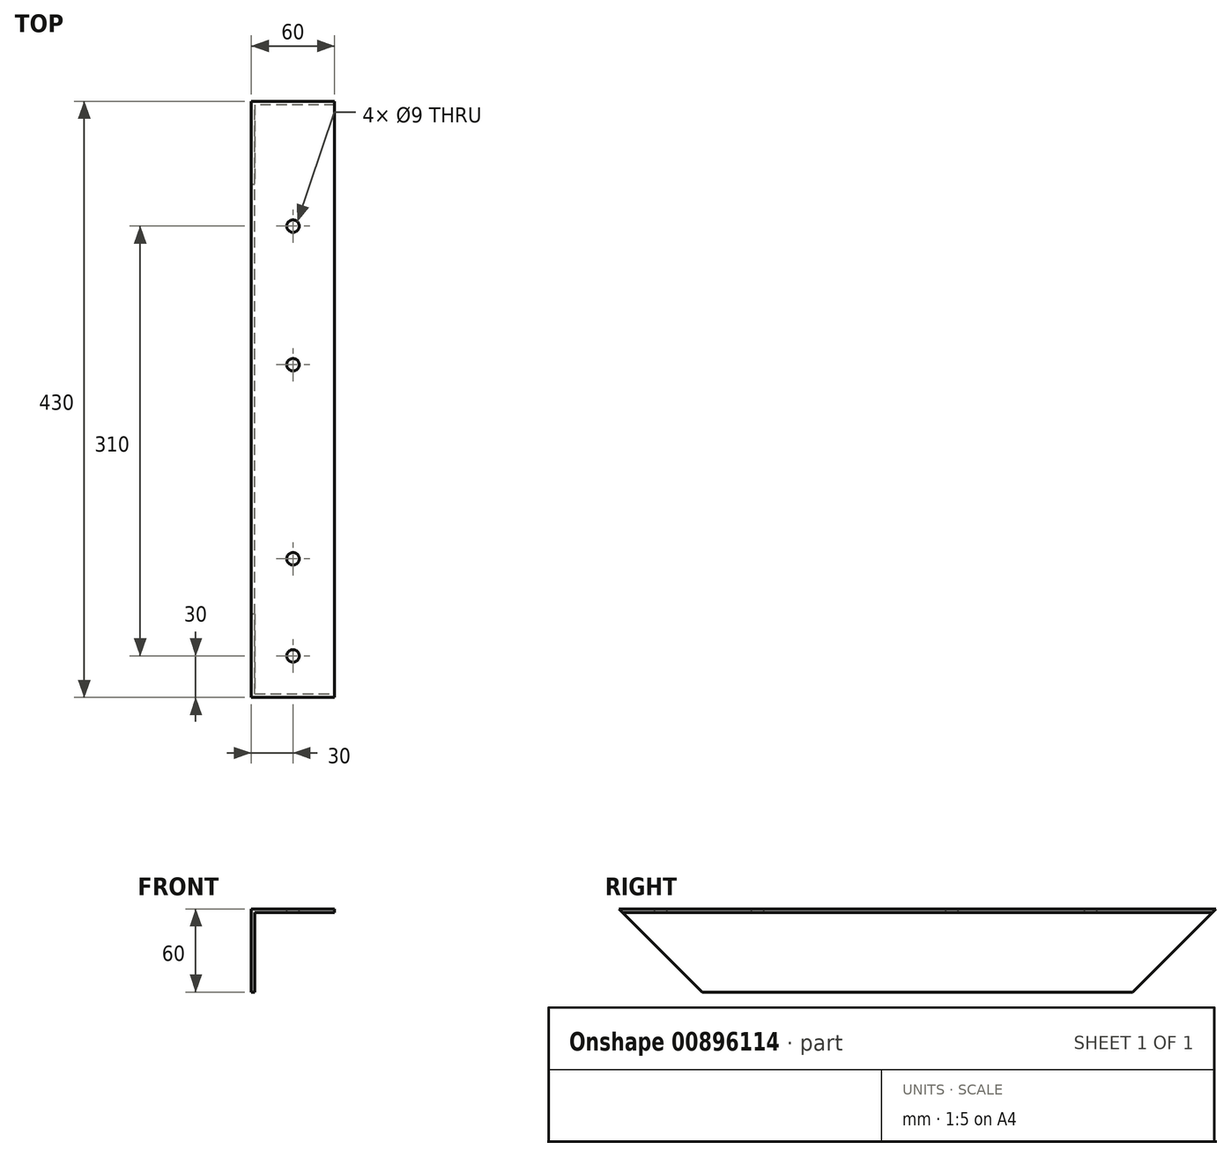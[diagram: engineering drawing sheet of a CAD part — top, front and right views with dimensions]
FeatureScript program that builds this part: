
annotation { "Feature Type Name" : "Feature", "Feature Type Description" : "" }
export const myFeature = defineFeature(function(context is Context, id is Id, definition is map)
    precondition{}
    {
        {
            var Q0;
            Q0=qCreatedBy(makeId("Front.planeOp"),FACE);
            var sketch = newSketch(context, id + "F0", { "sketchPlane" : qUnion([Q0])});
            skLineSegment(sketch, "E0", {"start": v(0, 0) * mm, "end": v(60, 0) * mm});
            skLineSegment(sketch, "E1", {"start": v(60, 0) * mm, "end": v(60, -2.5) * mm});
            skLineSegment(sketch, "E2", {"start": v(60, -2.5) * mm, "end": v(2.5, -2.5) * mm});
            skLineSegment(sketch, "E3", {"start": v(2.5, -2.5) * mm, "end": v(2.5, -60) * mm});
            skLineSegment(sketch, "E4", {"start": v(2.5, -60) * mm, "end": v(0, -60) * mm});
            skLineSegment(sketch, "E5", {"start": v(0, -60) * mm, "end": v(0, 0) * mm});
            skSolve(sketch);
        }
        {
            var Q0;
            Q0=qSketchRegion(id+"F0",true);
            extrude(context, id + "F1", {"entities" : qUnion([Q0]), "depth" : 430 * mm, "offsetDistance" : 25 * mm});
        }
        {
            var Q0;
            Q0=makeQuery(id+"F1.opExtrude","SWEPT_FACE",FACE,{"disambiguationData":[OSD([sQuery(id+"F0.wireOp",EDGE,"E5")])]});
            var sketch = newSketch(context, id + "F2", { "sketchPlane" : qUnion([Q0])});
            skLineSegment(sketch, "E6", {"start": v(0, -60) * mm, "end": v(60, -60) * mm});
            skLineSegment(sketch, "E7", {"start": v(60, -60) * mm, "end": v(0, 0) * mm});
            skLineSegment(sketch, "E8", {"start": v(0, 0) * mm, "end": v(0, -60) * mm});
            skLineSegment(sketch, "E9", {"start": v(430, -60) * mm, "end": v(430, 0) * mm});
            skLineSegment(sketch, "E10", {"start": v(430, 0) * mm, "end": v(370, -60) * mm});
            skLineSegment(sketch, "E11", {"start": v(370, -60) * mm, "end": v(430, -60) * mm});
            skSolve(sketch);
        }
        {
            var Q0;
            Q0 = qSketchRegion(id + "F2", true);
            extrude(context, id + "F3", {"entities" : qUnion([Q0]), "operationType" : NewBodyOperationType.REMOVE, "endBound" : BoundingType.THROUGH_ALL, "oppositeDirection" : true, "depth" : 25 * mm, "offsetDistance" : 25 * mm});
        }
        {
            var Q0;
            Q0=makeQuery(id+"F1.opExtrude","SWEPT_FACE",FACE,{"disambiguationData":[OSD([sQuery(id+"F0.wireOp",EDGE,"E0")])]});
            var sketch = newSketch(context, id + "F4", { "sketchPlane" : qUnion([Q0])});
            skLineSegment(sketch, "E12", {"start": v(30, 0) * mm, "end": v(30, -90) * mm, "construction": true});
            skLineSegment(sketch, "E13", {"start": v(30, -90) * mm, "end": v(30, -190) * mm, "construction": true});
            skCircle(sketch, "E14", {"center": v(30, -90) * mm, "radius": 4.5 * mm});
            skCircle(sketch, "E15", {"center": v(30, -190) * mm, "radius": 4.5 * mm});
            skLineSegment(sketch, "E16", {"start": v(30, -190) * mm, "end": v(30, -330) * mm, "construction": true});
            skLineSegment(sketch, "E17", {"start": v(30, -330) * mm, "end": v(30, -400) * mm, "construction": true});
            skLineSegment(sketch, "E18", {"start": v(30, -400) * mm, "end": v(30, -430) * mm, "construction": true});
            skCircle(sketch, "E19", {"center": v(30, -330) * mm, "radius": 4.5 * mm});
            skCircle(sketch, "E20", {"center": v(30, -400) * mm, "radius": 4.5 * mm});
            skSolve(sketch);
        }
        {
            var Q0;
            Q0 = qSketchRegion(id + "F4", true);
            extrude(context, id + "F5", {"entities" : qUnion([Q0]), "operationType" : NewBodyOperationType.REMOVE, "endBound" : BoundingType.THROUGH_ALL, "oppositeDirection" : true, "depth" : 25 * mm, "offsetDistance" : 25 * mm});
        }
    });
